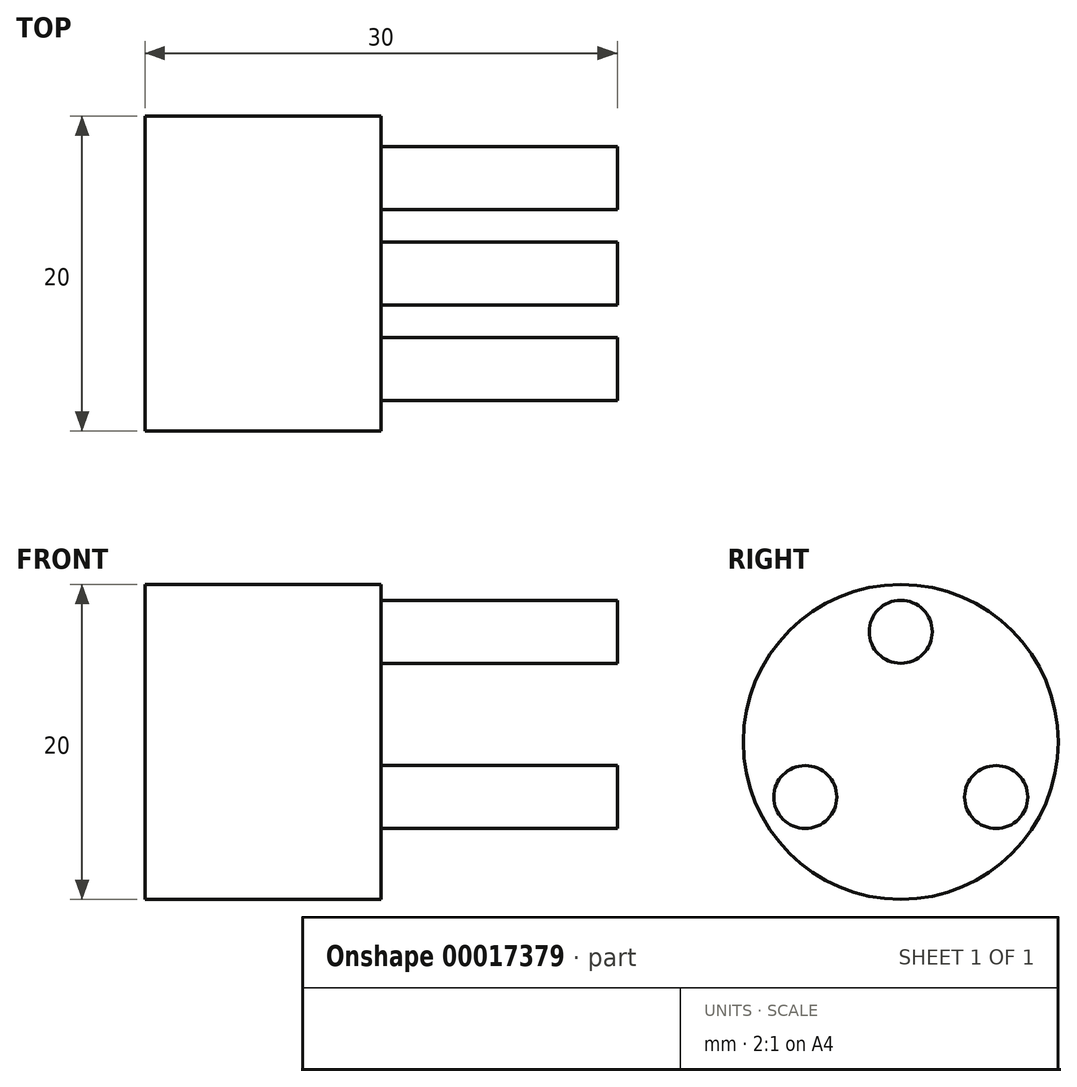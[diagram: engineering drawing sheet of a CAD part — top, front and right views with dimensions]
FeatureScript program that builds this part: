
annotation { "Feature Type Name" : "Feature", "Feature Type Description" : "" }
export const myFeature = defineFeature(function(context is Context, id is Id, definition is map)
    precondition{}
    {
        {
            var Q0;
            Q0=qCreatedBy(makeId("Right.planeOp"),FACE);
            var sketch = newSketch(context, id + "F0", { "sketchPlane" : qUnion([Q0])});
            skCircle(sketch, "E0", {"center": v(0, 0) * mm, "radius": 10 * mm});
            skLineSegment(sketch, "E1", {"start": v(0, 0) * mm, "end": v(10, 0) * mm});
            skSolve(sketch);
        }
        {
            var Q0;
            Q0=qSketchRegion(id+"F0",true);
            extrude(context, id + "F1", {"entities" : qUnion([Q0]), "depth" : 15 * mm});
        }
        {
            var Q0;
            Q0=makeQuery(id+"F1.opExtrude","CAP_FACE",FACE,{"disambiguationData":[OSD([sQuery(id+"F0.wireOp",EDGE,"E0")])],"isStart":false});
            var sketch = newSketch(context, id + "F2", { "sketchPlane" : qUnion([Q0])});
            skLineSegment(sketch, "E2", {"start": v(0, 5) * mm, "end": v(0, 7) * mm});
            skCircle(sketch, "E3", {"center": v(0, 7) * mm, "radius": 2 * mm});
            skLineSegment(sketch, "E4", {"start": v(0, 7) * mm, "end": v(2, 7) * mm});
            skCircle(sketch, "E5", {"center": v(6.06, -3.5) * mm, "radius": 2 * mm});
            skCircle(sketch, "E6", {"center": v(-6.06, -3.5) * mm, "radius": 2 * mm});
            skSolve(sketch);
        }
        {
            var Q0;
            Q0=qSketchRegion(id+"F2",true);
            extrude(context, id + "F3", {"entities" : qUnion([Q0]), "operationType" : NewBodyOperationType.ADD, "depth" : 15 * mm});
        }
    });
